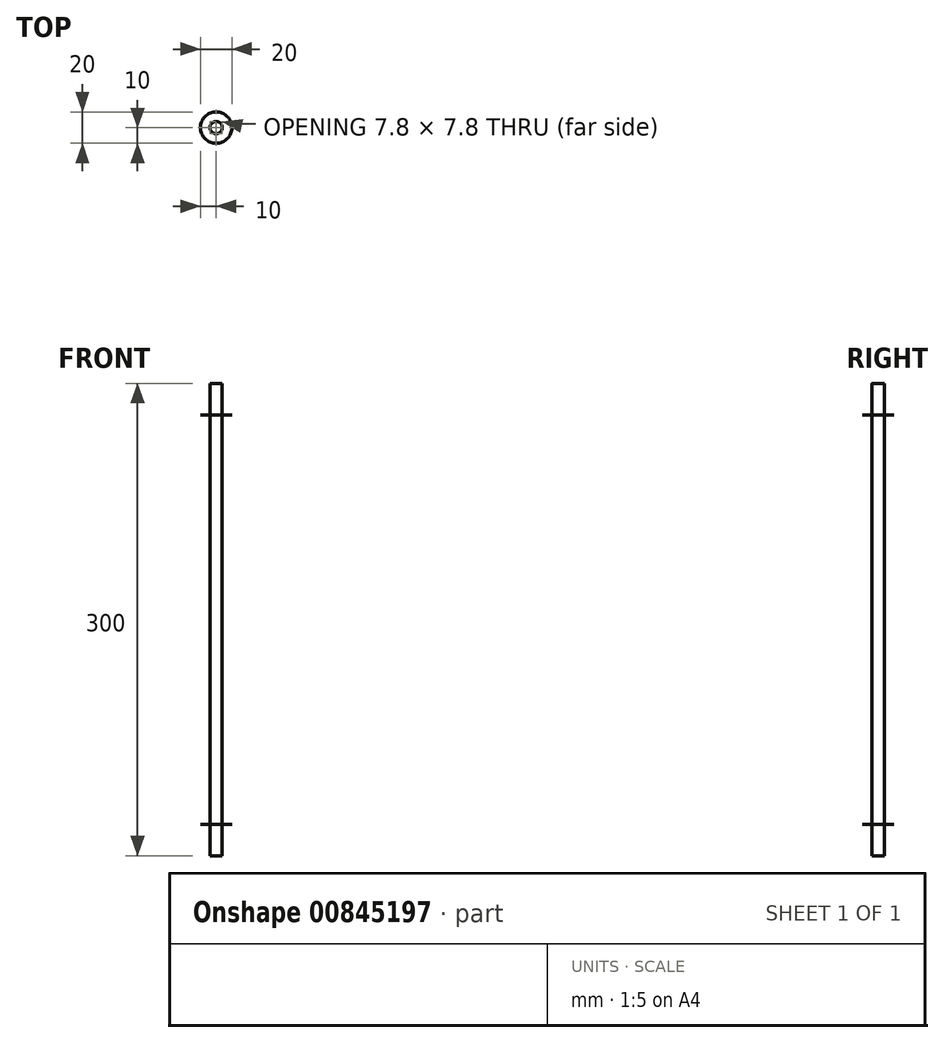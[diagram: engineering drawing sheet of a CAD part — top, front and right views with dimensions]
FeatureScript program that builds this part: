
annotation { "Feature Type Name" : "Feature", "Feature Type Description" : "" }
export const myFeature = defineFeature(function(context is Context, id is Id, definition is map)
    precondition{}
    {
        {
            var Q0;
            Q0=qCreatedBy(makeId("Top.planeOp"),FACE);
            var sketch = newSketch(context, id + "F0", { "sketchPlane" : qUnion([Q0])});
            skCircle(sketch, "E0", {"center": v(0, 0) * mm, "radius": 3.9 * mm});
            skSolve(sketch);
        }
        {
            var Q0;
            Q0=makeQuery(id+"F0.imprint","IMPRINT",FACE,{"disambiguationData":[TD([[makeQuery(id+"F0.imprint","IMPRINT",EDGE,{"derivedFrom":sQuery(id+"F0.wireOp",EDGE,"E0")}),1.0]])]});
            extrude(context, id + "F1", {"entities" : qUnion([Q0]), "oppositeDirection" : true, "depth" : 300 * mm, "offsetDistance" : 25 * mm});
        }
        {
            var Q0;
            Q0=makeQuery(id+"F1.opExtrude","CAP_FACE",FACE,{"disambiguationData":[OSD([sQuery(id+"F0.wireOp",EDGE,"E0")])],"isStart":false});
            cPlane(context, id + "F2", {"entities" : qUnion([Q0]), "cplaneType" : CPlaneType.OFFSET, "offset" : 20 * mm, "oppositeDirection" : true, "width" : 150 * mm, "height" : 150 * mm});
        }
        {
            var Q0;
            Q0=qCreatedBy(id+"F2.planeOp",FACE);
            var sketch = newSketch(context, id + "F3", { "sketchPlane" : qUnion([Q0])});
            skCircle(sketch, "E1", {"center": v(0, 0) * mm, "radius": 10 * mm});
            skSolve(sketch);
        }
        {
            var Q0;
            Q0 = qSketchRegion(id + "F3", true);
            extrude(context, id + "F4", {"entities" : qUnion([Q0]), "operationType" : NewBodyOperationType.ADD, "oppositeDirection" : true, "depth" : 0 * mm, "offsetDistance" : 25 * mm});
        }
        {
            var Q0;
            Q0=makeQuery(id+"F0.imprint","IMPRINT",FACE,{"disambiguationData":[TD([[makeQuery(id+"F0.imprint","IMPRINT",EDGE,{"derivedFrom":sQuery(id+"F0.wireOp",EDGE,"E0")}),1.0]])]});
            cPlane(context, id + "F5", {"entities" : qUnion([Q0]), "cplaneType" : CPlaneType.OFFSET, "offset" : 20 * mm, "oppositeDirection" : true, "width" : 150 * mm, "height" : 150 * mm});
        }
        {
            var Q0;
            Q0=qCreatedBy(id+"F5.planeOp",FACE);
            var sketch = newSketch(context, id + "F6", { "sketchPlane" : qUnion([Q0])});
            skCircle(sketch, "E2", {"center": v(0, 0) * mm, "radius": 10 * mm});
            skSolve(sketch);
        }
        {
            var Q0;
            Q0 = qSketchRegion(id + "F6", true);
            extrude(context, id + "F7", {"entities" : qUnion([Q0]), "operationType" : NewBodyOperationType.ADD, "oppositeDirection" : true, "depth" : 0 * mm, "offsetDistance" : 25 * mm});
        }
    });
